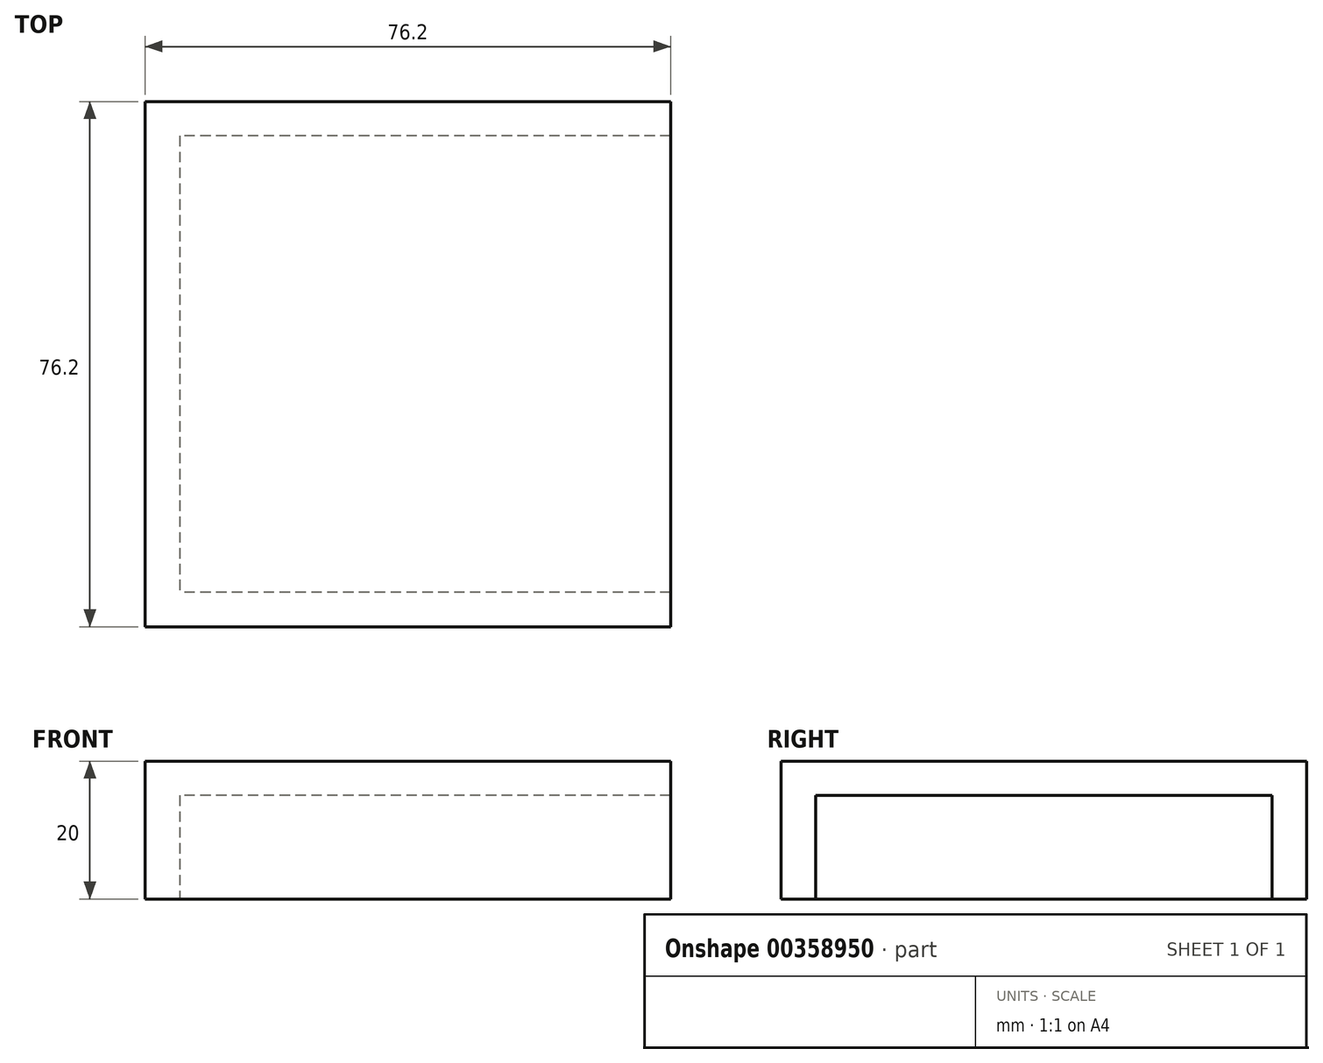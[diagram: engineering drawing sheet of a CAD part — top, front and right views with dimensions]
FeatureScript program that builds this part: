
annotation { "Feature Type Name" : "Feature", "Feature Type Description" : "" }
export const myFeature = defineFeature(function(context is Context, id is Id, definition is map)
    precondition{}
    {
        {
            var Q0;
            Q0=qCreatedBy(makeId("Top.planeOp"),FACE);
            var sketch = newSketch(context, id + "F0", { "sketchPlane" : qUnion([Q0])});
            skLineSegment(sketch, "E0.bottom", {"start": v(38.1, 38.1) * mm, "end": v(-38.1, 38.1) * mm});
            skLineSegment(sketch, "E0.top", {"start": v(38.1, -38.1) * mm, "end": v(-38.1, -38.1) * mm});
            skLineSegment(sketch, "E0.left", {"start": v(38.1, 38.1) * mm, "end": v(38.1, -38.1) * mm});
            skLineSegment(sketch, "E0.right", {"start": v(-38.1, 38.1) * mm, "end": v(-38.1, -38.1) * mm});
            skPoint(sketch, "E0.middle", {"position": v(0, 0) * mm});
            skSolve(sketch);
        }
        {
            var Q0;
            Q0 = qSketchRegion(id + "F0", true);
            extrude(context, id + "F1", {"entities" : qUnion([Q0]), "depth" : 20 * mm});
        }
        {
            var Q0;
            Q0=makeQuery(id+"F1.opExtrude","CAP_FACE",FACE,{"disambiguationData":[OSD([sQuery(id+"F0.wireOp",EDGE,"E0.bottom"),sQuery(id+"F0.wireOp",EDGE,"E0.top"),sQuery(id+"F0.wireOp",EDGE,"E0.left"),sQuery(id+"F0.wireOp",EDGE,"E0.right")])],"isStart":true});
            var Q1;
            Q1=makeQuery(id+"F1.opExtrude","SWEPT_FACE",FACE,{"disambiguationData":[OSD([sQuery(id+"F0.wireOp",EDGE,"E0.left")])]});
            shell(context, id + "F2", {"entities" : qUnion([Q0, Q1]), "thickness" : 5 * mm});
        }
    });
